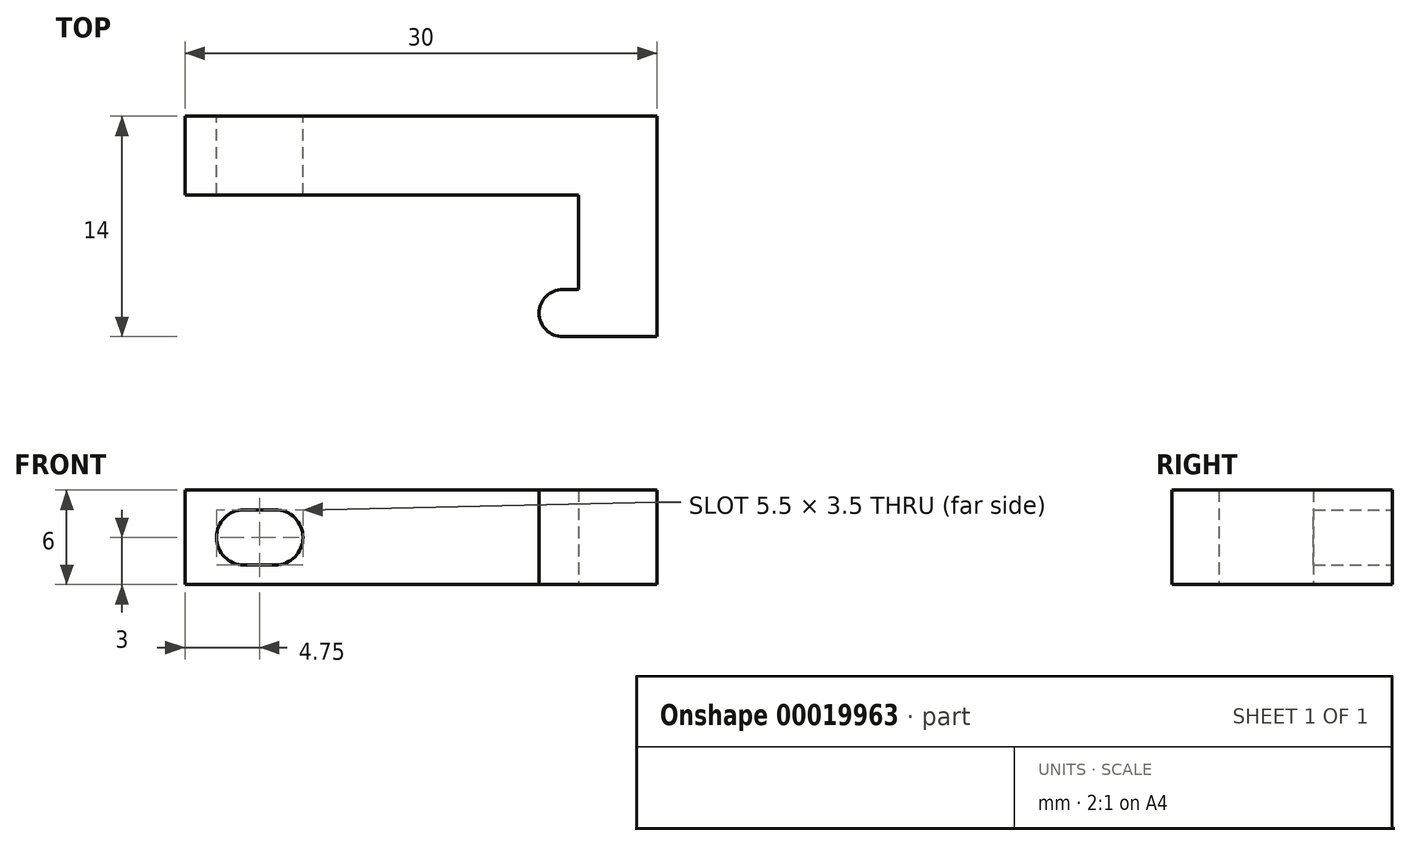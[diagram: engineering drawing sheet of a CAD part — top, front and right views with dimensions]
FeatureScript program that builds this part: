
annotation { "Feature Type Name" : "Feature", "Feature Type Description" : "" }
export const myFeature = defineFeature(function(context is Context, id is Id, definition is map)
    precondition{}
    {
        {
            var Q0;
            Q0=qCreatedBy(makeId("Top.planeOp"),FACE);
            var sketch = newSketch(context, id + "F0", { "sketchPlane" : qUnion([Q0])});
            skLineSegment(sketch, "E0", {"start": v(0, 0) * mm, "end": v(5, 0) * mm});
            skLineSegment(sketch, "E1", {"start": v(5, 0) * mm, "end": v(5, 14) * mm});
            skLineSegment(sketch, "E2", {"start": v(5, 14) * mm, "end": v(-25, 14) * mm});
            skLineSegment(sketch, "E3", {"start": v(-25, 14) * mm, "end": v(-25, 9) * mm});
            skLineSegment(sketch, "E4", {"start": v(-25, 9) * mm, "end": v(0, 9) * mm});
            skLineSegment(sketch, "E5", {"start": v(0, 9) * mm, "end": v(0, 3) * mm});
            skLineSegment(sketch, "E6", {"start": v(0, 3) * mm, "end": v(-1, 3) * mm});
            skLineSegment(sketch, "E7", {"start": v(0, 0) * mm, "end": v(-1, 0) * mm});
            skArc(sketch, "E8", {"start": v(-1, 3) * mm, "mid": v(-2.5, 1.5) * mm, "end": v(-1, 0) * mm});
            skSolve(sketch);
        }
        {
            var Q0;
            Q0=qSketchRegion(id+"F0",true);
            extrude(context, id + "F1", {"entities" : qUnion([Q0]), "depth" : 6 * mm});
        }
        {
            var Q0;
            Q0=makeQuery(id+"F1.opExtrude","SWEPT_FACE",FACE,{"disambiguationData":[OSD([sQuery(id+"F0.wireOp",EDGE,"E2")])]});
            var sketch = newSketch(context, id + "F2", { "sketchPlane" : qUnion([Q0])});
            skCircle(sketch, "E9", {"center": v(21.25, 3) * mm, "radius": 1.75 * mm});
            skLineSegment(sketch, "E10", {"start": v(21.25, 6) * mm, "end": v(21.25, 0) * mm});
            skCircle(sketch, "E11", {"center": v(19.25, 3) * mm, "radius": 1.75 * mm});
            skLineSegment(sketch, "E12", {"start": v(19.25, 4.75) * mm, "end": v(21.25, 4.75) * mm});
            skLineSegment(sketch, "E13", {"start": v(19.25, 1.25) * mm, "end": v(21.25, 1.25) * mm});
            skSolve(sketch);
        }
        {
            var Q0;
            Q0=qSketchRegion(id+"F2",true);
            var Q1;
            {var subQ0=sQuery(id+"F2.wireOp",EDGE,"E11");var subQ1=sQuery(id+"F2.wireOp",EDGE,"E9");var subQ3=makeQuery(id+"F2.imprint","INTERSECT",VERTEX,{"disambiguationData":[OD(0.0)],"derivedFrom":[subQ1,subQ0]});Q1=makeQuery(id+"F2.imprint","IMPRINT",FACE,{"disambiguationData":[TD([[makeQuery(id+"F2.imprint","IMPRINT",EDGE,{"disambiguationData":[TD([[subQ3,-1.0]])],"derivedFrom":subQ1}),1.0]])]});}
            extrude(context, id + "F3", {"entities" : qUnion([Q0, Q1]), "operationType" : NewBodyOperationType.REMOVE, "oppositeDirection" : true, "depth" : 25 * mm});
        }
    });
